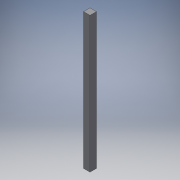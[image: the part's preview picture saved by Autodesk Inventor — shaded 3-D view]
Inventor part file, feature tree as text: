
AUTODESK INVENTOR PART (.ipt)
format: ipt  version: 2017 (Build 210142000, 142)  size: 91,648 bytes
history: native  units: mm
features: extrude x1, sketch x1
ambient origin geometry x8: Origin, YZ Plane, XZ Plane, XY Plane, X Axis, Y Axis, Z Axis, Center Point
bodies: Solid1 (feature_tree)
feature tree (2):
  extrude  "Extrusion1"  Depth=200.0mm TaperAngle=0.0deg
  sketch  "Sketch1"  dims[d0=9.525mm d1=200.0mm d2=0.0mm]
